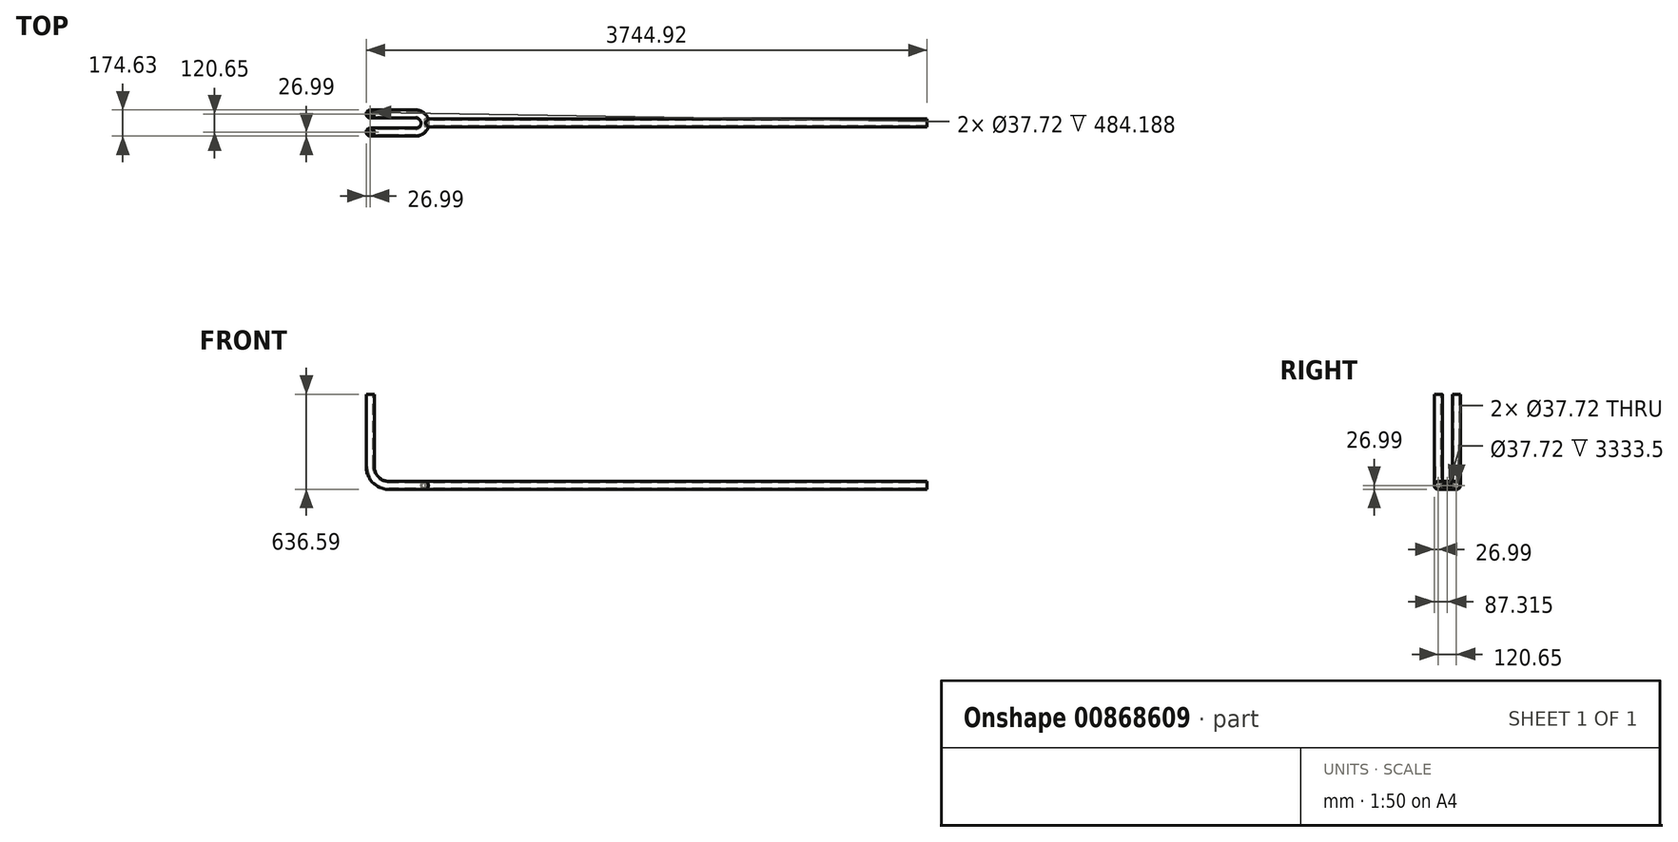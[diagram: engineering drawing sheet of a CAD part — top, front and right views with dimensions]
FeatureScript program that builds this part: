
annotation { "Feature Type Name" : "Feature", "Feature Type Description" : "" }
export const myFeature = defineFeature(function(context is Context, id is Id, definition is map)
    precondition{}
    {
        {
            var Q0;
            Q0=qCreatedBy(makeId("Front.planeOp"),FACE);
            var sketch = newSketch(context, id + "F0", { "sketchPlane" : qUnion([Q0])});
            skLineSegment(sketch, "E0", {"start": v(0, 125.41) * mm, "end": v(0, 609.6) * mm});
            skLineSegment(sketch, "E1", {"start": v(125.41, 0) * mm, "end": v(304.8, 0) * mm});
            skPoint(sketch, "E2.visualSharp", {"position": v(0, 0) * mm});
            skArc(sketch, "E3.filletArc", {"start": v(0, 125.41) * mm, "mid": v(36.73, 36.73) * mm, "end": v(125.41, 0) * mm});
            skSolve(sketch);
        }
        {
            var Q0;
            Q0=qCreatedBy(makeId("Front.planeOp"),FACE);
            cPlane(context, id + "F1", {"entities" : qUnion([Q0]), "cplaneType" : CPlaneType.OFFSET, "offset" : 120.65 * mm, "width" : 152.4 * mm, "height" : 152.4 * mm});
        }
        {
            var Q0;
            Q0=qCreatedBy(id+"F1.planeOp",FACE);
            var sketch = newSketch(context, id + "F2", { "sketchPlane" : qUnion([Q0])});
            skLineSegment(sketch, "E4.0", {"start": v(125.41, 0) * mm, "end": v(304.8, 0) * mm});
            skArc(sketch, "E4.1", {"start": v(0, 125.41) * mm, "mid": v(36.73, 36.73) * mm, "end": v(125.41, 0) * mm});
            skLineSegment(sketch, "E4.2", {"start": v(0, 125.41) * mm, "end": v(0, 609.6) * mm});
            skSolve(sketch);
        }
        {
            var Q0;
            Q0=qCreatedBy(makeId("Top.planeOp"),FACE);
            var sketch = newSketch(context, id + "F3", { "sketchPlane" : qUnion([Q0])});
            skPoint(sketch, "E5.0", {"position": v(304.8, -120.65) * mm});
            skPoint(sketch, "E5.1", {"position": v(304.8, 0) * mm});
            skArc(sketch, "E6", {"start": v(304.8, -120.65) * mm, "mid": v(365.13, -60.33) * mm, "end": v(304.8, 0) * mm});
            skLineSegment(sketch, "E7", {"start": v(304.8, -120.65) * mm, "end": v(304.8, 0) * mm, "construction": true});
            skPoint(sketch, "E8", {"position": v(365.13, -60.32) * mm});
            skSolve(sketch);
        }
        {
            var Q0;
            Q0=sQuery(id+"F2.wireOp",VERTEX,"E4.2.end");
            var Q1;
            Q1=qCreatedBy(makeId("Top.planeOp"),FACE);
            cPlane(context, id + "F4", {"entities" : qUnion([Q0, Q1]), "cplaneType" : CPlaneType.PLANE_POINT, "offset" : 25.4 * mm, "width" : 152.4 * mm, "height" : 152.4 * mm});
        }
        {
            var Q0;
            Q0=qCreatedBy(id+"F4.planeOp",FACE);
            var sketch = newSketch(context, id + "F5", { "sketchPlane" : qUnion([Q0])});
            skCircle(sketch, "E9", {"center": v(0, 0) * mm, "radius": 18.86 * mm});
            skCircle(sketch, "E10", {"center": v(0, 0) * mm, "radius": 26.99 * mm});
            skSolve(sketch);
        }
        {
            var Q0;
            Q0=makeQuery(id+"F5.imprint","IMPRINT",FACE,{"disambiguationData":[TD([[makeQuery(id+"F5.imprint","IMPRINT",EDGE,{"derivedFrom":sQuery(id+"F5.wireOp",EDGE,"E9")}),-1.0]])]});
            var Q1;
            Q1=sQuery(id+"F0.wireOp",EDGE,"E0");
            var Q2;
            Q2=sQuery(id+"F0.wireOp",EDGE,"E3.filletArc");
            var Q3;
            Q3=sQuery(id+"F0.wireOp",EDGE,"E1");
            var Q4;
            Q4=sQuery(id+"F3.wireOp",EDGE,"E6");
            var Q5;
            Q5=sQuery(id+"F2.wireOp",EDGE,"E4.0");
            var Q6;
            Q6=sQuery(id+"F2.wireOp",EDGE,"E4.1");
            var Q7;
            Q7=sQuery(id+"F2.wireOp",EDGE,"E4.2");
            sweep(context, id + "F6", {"profiles" : qUnion([Q0]), "path" : qUnion([Q1, Q2, Q3, Q4, Q5, Q6, Q7])});
        }
        {
            var Q0;
            Q0=qCreatedBy(makeId("Top.planeOp"),FACE);
            var sketch = newSketch(context, id + "F7", { "sketchPlane" : qUnion([Q0])});
            skPoint(sketch, "E11.0", {"position": v(365.13, -60.32) * mm});
            skLineSegment(sketch, "E12", {"start": v(365.12, -60.32) * mm, "end": v(3717.93, -60.32) * mm});
            skSolve(sketch);
        }
        {
            var Q0;
            Q0=sQuery(id+"F7.wireOp",VERTEX,"E12.end");
            var Q1;
            Q1=qCreatedBy(makeId("Right.planeOp"),FACE);
            cPlane(context, id + "F8", {"entities" : qUnion([Q0, Q1]), "cplaneType" : CPlaneType.PLANE_POINT, "offset" : 25.4 * mm, "width" : 152.4 * mm, "height" : 152.4 * mm});
        }
        {
            var Q0;
            Q0=qCreatedBy(id+"F8.planeOp",FACE);
            var sketch = newSketch(context, id + "F9", { "sketchPlane" : qUnion([Q0])});
            skPoint(sketch, "E13.0", {"position": v(-60.32, 0) * mm});
            skCircle(sketch, "E14", {"center": v(-60.32, 0) * mm, "radius": 18.86 * mm});
            skCircle(sketch, "E15", {"center": v(-60.32, 0) * mm, "radius": 26.99 * mm});
            skSolve(sketch);
        }
        {
            var Q0;
            Q0=makeQuery(id+"F9.imprint","IMPRINT",FACE,{"disambiguationData":[TD([[makeQuery(id+"F9.imprint","IMPRINT",EDGE,{"derivedFrom":sQuery(id+"F9.wireOp",EDGE,"E14")}),-1.0]])]});
            var Q1;
            Q1=sQuery(id+"F7.wireOp",EDGE,"E12");
            sweep(context, id + "F10", {"operationType" : NewBodyOperationType.ADD, "profiles" : qUnion([Q0]), "path" : qUnion([Q1])});
        }
    });
